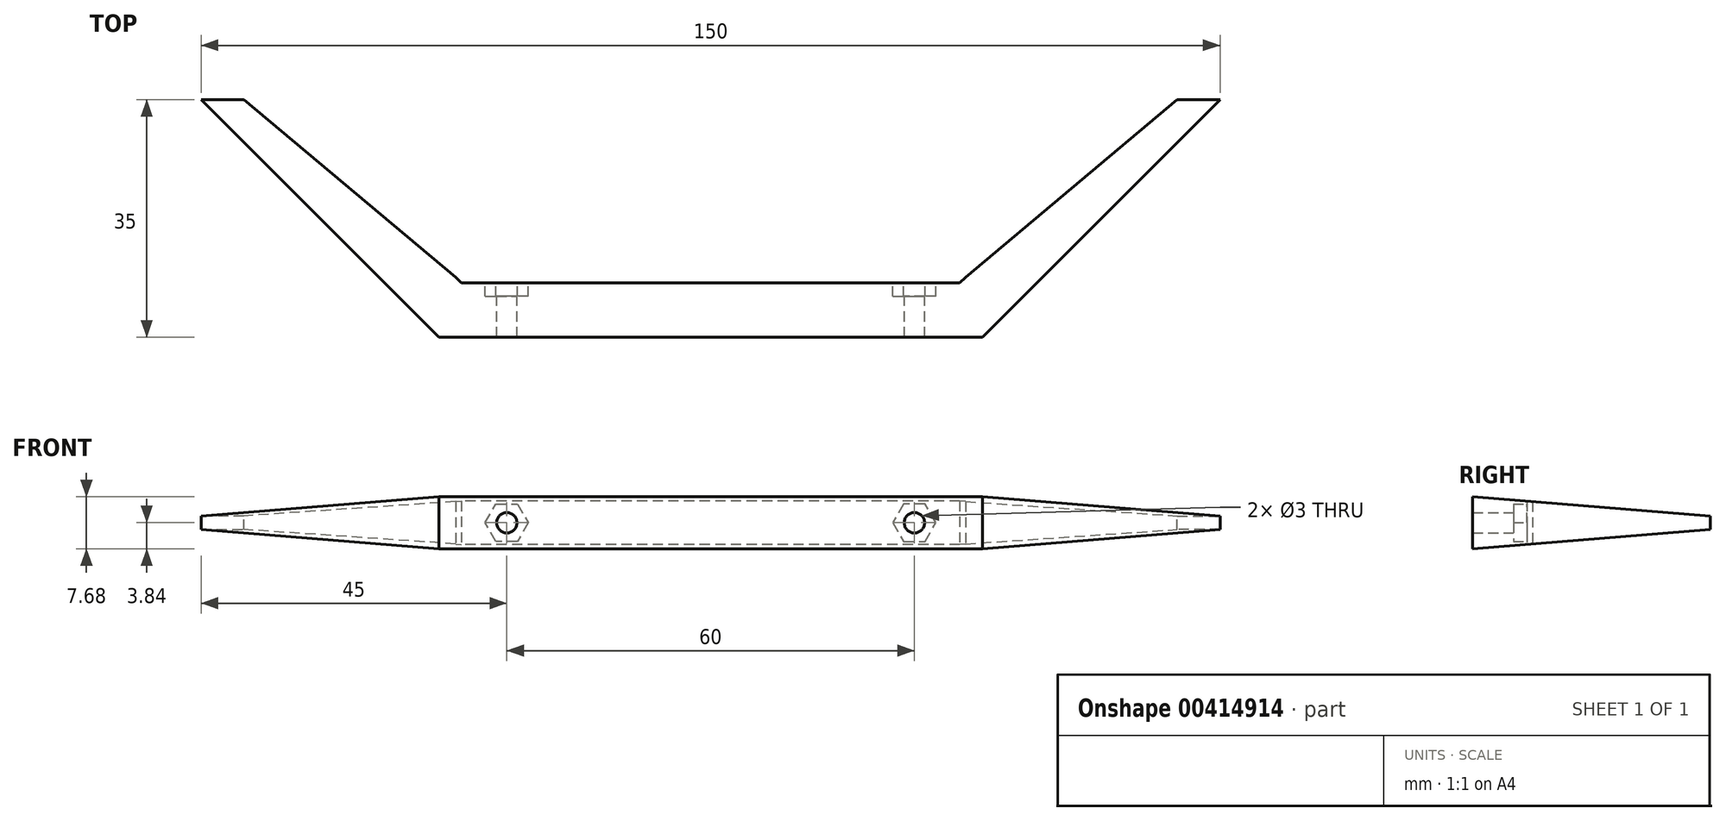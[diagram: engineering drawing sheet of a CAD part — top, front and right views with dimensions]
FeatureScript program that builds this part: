
annotation { "Feature Type Name" : "Feature", "Feature Type Description" : "" }
export const myFeature = defineFeature(function(context is Context, id is Id, definition is map)
    precondition{}
    {
        {
            var Q0;
            Q0=qCreatedBy(makeId("Top.planeOp"),FACE);
            var sketch = newSketch(context, id + "F0", { "sketchPlane" : qUnion([Q0])});
            skLineSegment(sketch, "E0.bottom", {"start": v(40, -4) * mm, "end": v(0, -4) * mm});
            skLineSegment(sketch, "E0.top", {"start": v(36.69, 4) * mm, "end": v(0, 4) * mm});
            skPoint(sketch, "E0.middle", {"position": v(0, 0) * mm});
            skLineSegment(sketch, "E1", {"start": v(63.69, 31) * mm, "end": v(75, 31) * mm});
            skLineSegment(sketch, "E2", {"start": v(40, -4) * mm, "end": v(75, 31) * mm});
            skLineSegment(sketch, "E3", {"start": v(36.69, 4) * mm, "end": v(63.69, 31) * mm});
            skPoint(sketch, "E0.left.end.orphan", {"position": v(40, 4) * mm});
            skLineSegment(sketch, "E4", {"start": v(0, 4) * mm, "end": v(0, -4) * mm});
            skPoint(sketch, "E4.endSnap0", {"position": v(0, -4) * mm});
            skPoint(sketch, "E0.right.end.orphan", {"position": v(-40, 4) * mm});
            skPoint(sketch, "E5.orphan", {"position": v(-40, -4) * mm});
            skPoint(sketch, "E6.orphan", {"position": v(0, 22.1) * mm});
            skPoint(sketch, "E7.orphan", {"position": v(0, -24.82) * mm});
            skSolve(sketch);
        }
        {
            var Q0;
            Q0 = qSketchRegion(id + "F0", true);
            extrude(context, id + "F1", {"entities" : qUnion([Q0]), "depth" : 8 * mm});
        }
        {
            var Q0;
            Q0=makeQuery(id+"F1.opExtrude","SWEPT_FACE",FACE,{"disambiguationData":[OSD([sQuery(id+"F0.wireOp",EDGE,"E0.top")])]});
            var sketch = newSketch(context, id + "F2", { "sketchPlane" : qUnion([Q0])});
            skCircle(sketch, "E8", {"center": v(-30, 4) * mm, "radius": 1.5 * mm});
            skCircle(sketch, "E9.cCircle", {"center": v(-30, 4) * mm, "radius": 2.75 * mm, "construction": true});
            skLineSegment(sketch, "E9.0", {"start": v(-26.82, 4) * mm, "end": v(-28.41, 1.25) * mm});
            skLineSegment(sketch, "E9.1", {"start": v(-28.41, 1.25) * mm, "end": v(-31.59, 1.25) * mm});
            skLineSegment(sketch, "E9.2", {"start": v(-31.59, 1.25) * mm, "end": v(-33.18, 4) * mm});
            skLineSegment(sketch, "E9.3", {"start": v(-33.18, 4) * mm, "end": v(-31.59, 6.75) * mm});
            skLineSegment(sketch, "E9.4", {"start": v(-31.59, 6.75) * mm, "end": v(-28.41, 6.75) * mm});
            skLineSegment(sketch, "E9.5", {"start": v(-28.41, 6.75) * mm, "end": v(-26.82, 4) * mm});
            skPoint(sketch, "E9.0.midPoint", {"position": v(-27.62, 2.62) * mm});
            skSolve(sketch);
        }
        {
            var Q0;
            Q0=makeQuery(id+"F2.imprint","IMPRINT",FACE,{"disambiguationData":[TD([[makeQuery(id+"F2.imprint","IMPRINT",EDGE,{"derivedFrom":sQuery(id+"F2.wireOp",EDGE,"E8")}),1.0]])]});
            extrude(context, id + "F3", {"entities" : qUnion([Q0]), "operationType" : NewBodyOperationType.REMOVE, "endBound" : BoundingType.UP_TO_NEXT, "oppositeDirection" : true, "depth" : 25 * mm});
        }
        {
            var Q0;
            Q0 = qSketchRegion(id + "F2", true);
            extrude(context, id + "F4", {"entities" : qUnion([Q0]), "operationType" : NewBodyOperationType.REMOVE, "oppositeDirection" : true, "depth" : 2 * mm});
        }
        {
            var Q0;
            Q0=makeQuery(id+"F1.opExtrude","SWEPT_EDGE",EDGE,{"disambiguationData":[OSD([sQuery(id+"F0.wireOp",EDGE,"E1"),sQuery(id+"F0.wireOp",EDGE,"E3")])]});
            chamfer(context, id + "F5", {"entities" : qUnion([Q0]), "chamferType" : ChamferType.TWO_OFFSETS, "width1" : 37 * mm, "oppositeDirection" : false, "width2" : 5 * mm, "tangentPropagation" : true});
        }
        {
            var Q0;
            Q0=makeQuery(id+"F1.opExtrude","CAP_EDGE",EDGE,{"disambiguationData":[OSD([sQuery(id+"F0.wireOp",EDGE,"E1")])],"isStart":true});
            var Q1;
            Q1=makeQuery(id+"F1.opExtrude","CAP_EDGE",EDGE,{"disambiguationData":[OSD([sQuery(id+"F0.wireOp",EDGE,"E1")])],"isStart":false});
            chamfer(context, id + "F6", {"entities" : qUnion([Q0, Q1]), "chamferType" : ChamferType.TWO_OFFSETS, "width1" : 37 * mm, "oppositeDirection" : false, "width2" : 3 * mm, "tangentPropagation" : true});
        }
        {
            var Q0;
            Q0=makeQuery(id+"F1.opExtrude","SWEPT_BODY",BODY,{"disambiguationData":[OSD([sQuery(id+"F0.wireOp",EDGE,"E0.bottom"),sQuery(id+"F0.wireOp",EDGE,"E0.top"),sQuery(id+"F0.wireOp",EDGE,"E1"),sQuery(id+"F0.wireOp",EDGE,"E2"),sQuery(id+"F0.wireOp",EDGE,"E3"),sQuery(id+"F0.wireOp",EDGE,"E4")])]});
            var Q1;
            Q1=qCreatedBy(makeId("Right.planeOp"),FACE);
            mirror(context, id + "F7", {"operationType" : NewBodyOperationType.ADD, "entities" : qUnion([Q0]), "mirrorPlane" : qUnion([Q1])});
        }
    });
